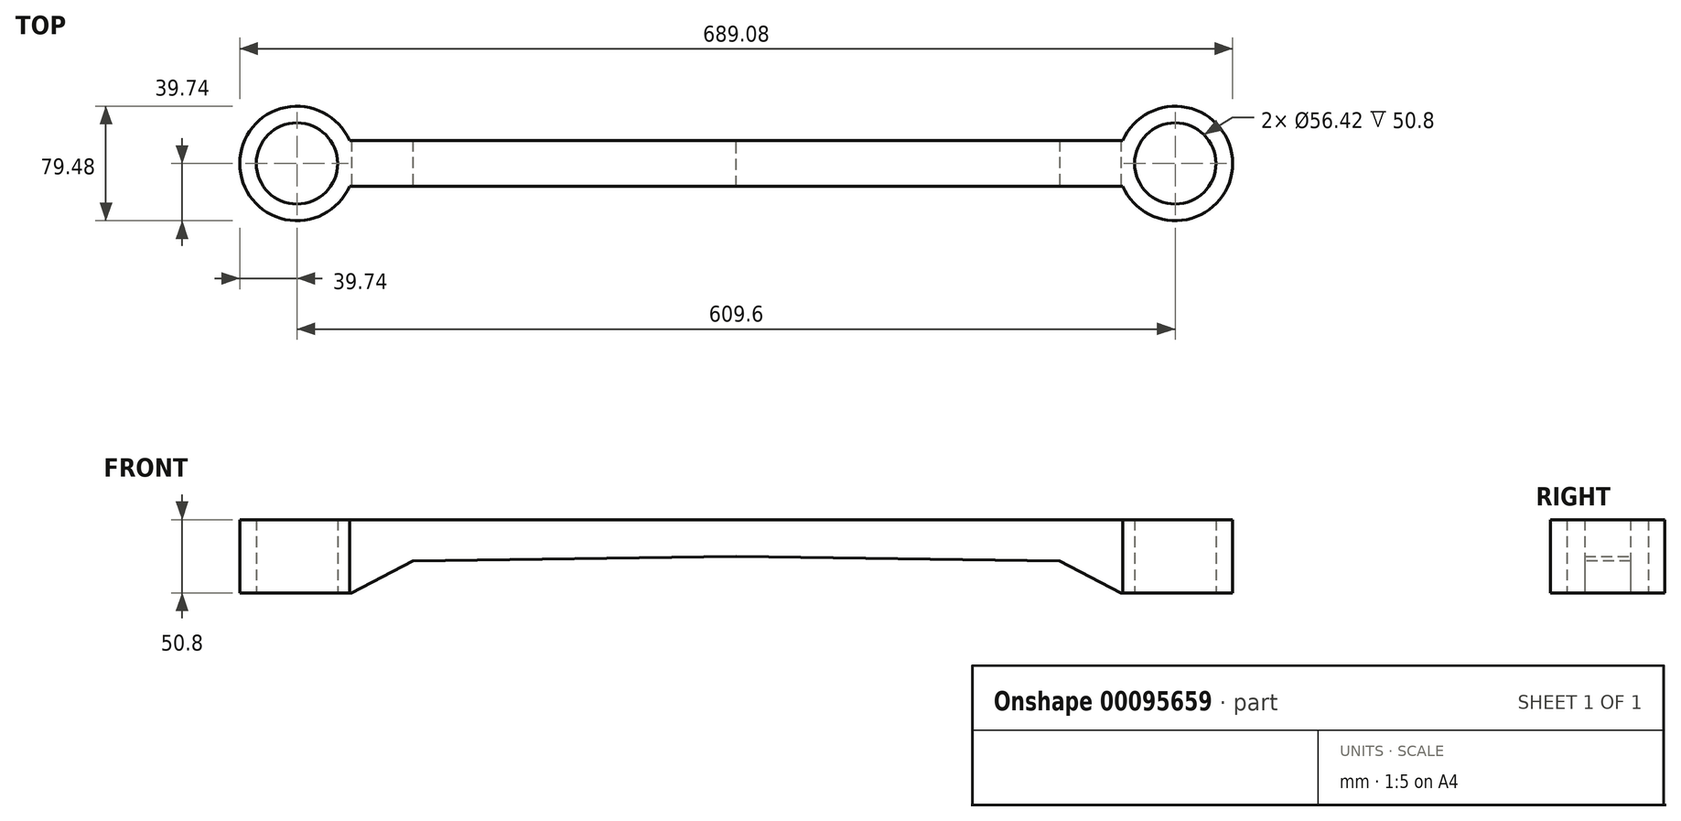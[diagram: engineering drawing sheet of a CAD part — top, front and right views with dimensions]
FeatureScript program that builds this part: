
annotation { "Feature Type Name" : "Feature", "Feature Type Description" : "" }
export const myFeature = defineFeature(function(context is Context, id is Id, definition is map)
    precondition{}
    {
        {
            var Q0;
            Q0=qCreatedBy(makeId("Top.planeOp"),FACE);
            var sketch = newSketch(context, id + "F0", { "sketchPlane" : qUnion([Q0])});
            skLineSegment(sketch, "E0.bottom", {"start": v(115.97, 15.88) * mm, "end": v(-152.4, 15.88) * mm});
            skLineSegment(sketch, "E0.top", {"start": v(115.97, -15.88) * mm, "end": v(-152.4, -15.88) * mm});
            skLineSegment(sketch, "E0.right", {"start": v(-152.4, 15.88) * mm, "end": v(-152.4, -15.88) * mm});
            skPoint(sketch, "E0.middle", {"position": v(0, 0) * mm});
            skCircle(sketch, "E1", {"center": v(152.4, 0) * mm, "radius": 28.21 * mm});
            skCircle(sketch, "E2", {"center": v(152.4, 0) * mm, "radius": 39.74 * mm});
            skPoint(sketch, "E3.orphan", {"position": v(152.4, 15.88) * mm});
            skPoint(sketch, "E4.orphan", {"position": v(152.4, -15.88) * mm});
            skSolve(sketch);
        }
        {
            var Q0;
            Q0 = qSketchRegion(id + "F0", true);
            extrude(context, id + "F1", {"entities" : qUnion([Q0]), "depth" : 25.4 * mm, "hasSecondDirection" : true, "secondDirectionOppositeDirection" : true, "secondDirectionDepth" : 25.4 * mm});
        }
        {
            var Q0;
            Q0=qCreatedBy(makeId("Front.planeOp"),FACE);
            var sketch = newSketch(context, id + "F2", { "sketchPlane" : qUnion([Q0])});
            skLineSegment(sketch, "E5", {"start": v(-164.03, 0) * mm, "end": v(72.03, -3.34) * mm});
            skLineSegment(sketch, "E6", {"start": v(72.03, -3.34) * mm, "end": v(115.61, -25.93) * mm});
            skLineSegment(sketch, "E7", {"start": v(115.61, -25.93) * mm, "end": v(115.61, -51.7) * mm});
            skLineSegment(sketch, "E8", {"start": v(115.61, -51.7) * mm, "end": v(-162.44, -48.52) * mm});
            skLineSegment(sketch, "E9", {"start": v(-162.44, -48.52) * mm, "end": v(-164.03, 0) * mm});
            skSolve(sketch);
        }
        {
            var Q0;
            Q0 = qSketchRegion(id + "F2", true);
            extrude(context, id + "F3", {"entities" : qUnion([Q0]), "operationType" : NewBodyOperationType.REMOVE, "oppositeDirection" : true, "depth" : 67.7 * mm, "hasSecondDirection" : true, "secondDirectionOppositeDirection" : false, "secondDirectionDepth" : 44.95 * mm});
        }
        {
            var Q0;
            Q0=makeQuery(id+"F1.opExtrude","SWEPT_BODY",BODY,{"disambiguationData":[OSD([sQuery(id+"F0.wireOp",EDGE,"E0.bottom"),sQuery(id+"F0.wireOp",EDGE,"E0.top"),sQuery(id+"F0.wireOp",EDGE,"E0.right"),sQuery(id+"F0.wireOp",EDGE,"E1"),sQuery(id+"F0.wireOp",EDGE,"E2")])]});
            var Q1;
            Q1=makeQuery(id+"F1.opExtrude","SWEPT_FACE",FACE,{"disambiguationData":[OSD([sQuery(id+"F0.wireOp",EDGE,"E0.right")])]});
            mirror(context, id + "F4", {"operationType" : NewBodyOperationType.ADD, "entities" : qUnion([Q0]), "mirrorPlane" : qUnion([Q1])});
        }
    });
